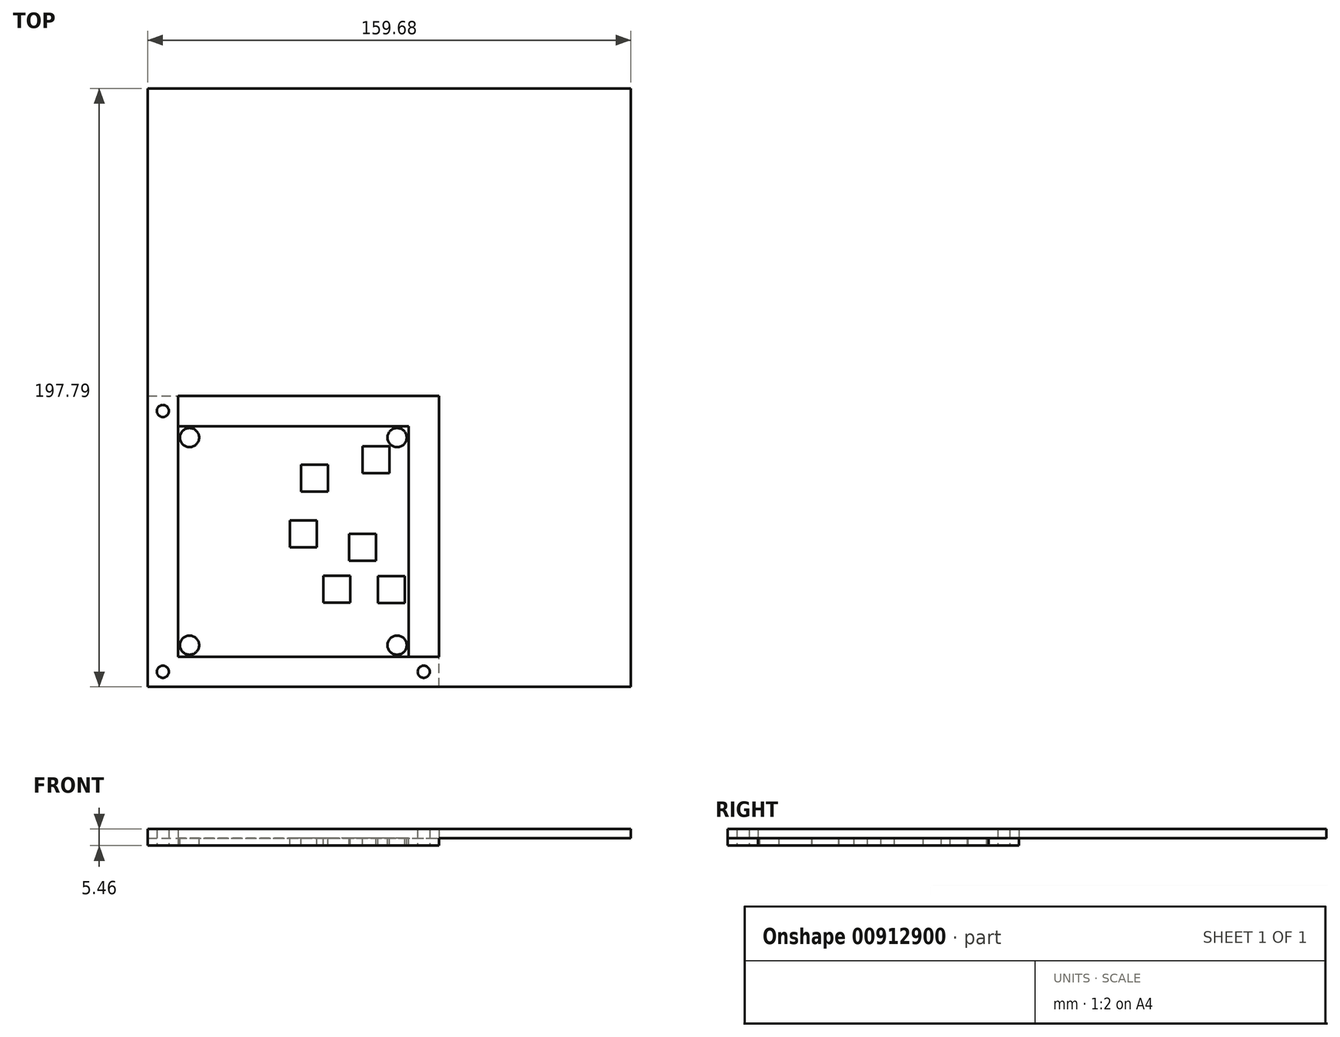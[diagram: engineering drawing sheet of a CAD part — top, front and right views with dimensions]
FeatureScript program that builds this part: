
annotation { "Feature Type Name" : "Feature", "Feature Type Description" : "" }
export const myFeature = defineFeature(function(context is Context, id is Id, definition is map)
    precondition{}
    {
        {
            var Q0;
            Q0=qCreatedBy(makeId("Top.planeOp"),FACE);
            var sketch = newSketch(context, id + "F0", { "sketchPlane" : qUnion([Q0])});
            skLineSegment(sketch, "E0.bottom", {"start": v(-59.12, -65.9) * mm, "end": v(37.08, -65.9) * mm});
            skLineSegment(sketch, "E0.top", {"start": v(-59.12, 30.3) * mm, "end": v(37.08, 30.3) * mm});
            skLineSegment(sketch, "E0.left", {"start": v(-59.12, -65.9) * mm, "end": v(-59.12, 30.3) * mm});
            skLineSegment(sketch, "E0.right", {"start": v(37.08, -65.9) * mm, "end": v(37.08, 30.3) * mm});
            skLineSegment(sketch, "E1.bottom", {"start": v(-59.12, -65.9) * mm, "end": v(-49.12, -65.9) * mm});
            skLineSegment(sketch, "E1.top", {"start": v(-59.12, -55.9) * mm, "end": v(-49.12, -55.9) * mm});
            skLineSegment(sketch, "E1.left", {"start": v(-59.12, -65.9) * mm, "end": v(-59.12, -55.9) * mm});
            skLineSegment(sketch, "E1.right", {"start": v(-49.12, -65.9) * mm, "end": v(-49.12, -55.9) * mm});
            skLineSegment(sketch, "E2.bottom", {"start": v(-49.12, -55.9) * mm, "end": v(27.08, -55.9) * mm});
            skLineSegment(sketch, "E2.top", {"start": v(-49.12, 20.3) * mm, "end": v(27.08, 20.3) * mm});
            skLineSegment(sketch, "E2.left", {"start": v(-49.12, -55.9) * mm, "end": v(-49.12, 20.3) * mm});
            skLineSegment(sketch, "E2.right", {"start": v(27.08, -55.9) * mm, "end": v(27.08, 20.3) * mm});
            skLineSegment(sketch, "E3.bottom", {"start": v(37.08, -65.9) * mm, "end": v(27.08, -65.9) * mm});
            skLineSegment(sketch, "E3.top", {"start": v(37.08, -55.9) * mm, "end": v(27.08, -55.9) * mm});
            skLineSegment(sketch, "E3.left", {"start": v(37.08, -65.9) * mm, "end": v(37.08, -55.9) * mm});
            skLineSegment(sketch, "E3.right", {"start": v(27.08, -65.9) * mm, "end": v(27.08, -55.9) * mm});
            skLineSegment(sketch, "E4.bottom", {"start": v(37.08, 30.3) * mm, "end": v(27.08, 30.3) * mm});
            skLineSegment(sketch, "E4.top", {"start": v(37.08, 20.3) * mm, "end": v(27.08, 20.3) * mm});
            skLineSegment(sketch, "E4.left", {"start": v(37.08, 30.3) * mm, "end": v(37.08, 20.3) * mm});
            skLineSegment(sketch, "E4.right", {"start": v(27.08, 30.3) * mm, "end": v(27.08, 20.3) * mm});
            skLineSegment(sketch, "E5.bottom", {"start": v(-59.12, 30.3) * mm, "end": v(-49.12, 30.3) * mm});
            skLineSegment(sketch, "E5.top", {"start": v(-59.12, 20.3) * mm, "end": v(-49.12, 20.3) * mm});
            skLineSegment(sketch, "E5.left", {"start": v(-59.12, 30.3) * mm, "end": v(-59.12, 20.3) * mm});
            skLineSegment(sketch, "E5.right", {"start": v(-49.12, 30.3) * mm, "end": v(-49.12, 20.3) * mm});
            skLineSegment(sketch, "E6.bottom", {"start": v(-59.12, 20.3) * mm, "end": v(-54.12, 20.3) * mm});
            skLineSegment(sketch, "E6.left", {"start": v(-59.12, 20.3) * mm, "end": v(-59.12, 25.3) * mm});
            skLineSegment(sketch, "E7.bottom", {"start": v(37.08, 20.3) * mm, "end": v(32.08, 20.3) * mm});
            skLineSegment(sketch, "E7.left", {"start": v(37.08, 20.3) * mm, "end": v(37.08, 25.3) * mm});
            skLineSegment(sketch, "E8.bottom", {"start": v(-59.12, -65.9) * mm, "end": v(-54.12, -65.9) * mm});
            skLineSegment(sketch, "E8.left", {"start": v(-59.12, -65.9) * mm, "end": v(-59.12, -60.9) * mm});
            skLineSegment(sketch, "E9.bottom", {"start": v(37.08, -65.9) * mm, "end": v(32.08, -65.9) * mm});
            skLineSegment(sketch, "E9.left", {"start": v(37.08, -65.9) * mm, "end": v(37.08, -60.9) * mm});
            skCircle(sketch, "E10", {"center": v(-54.12, 25.3) * mm, "radius": 2 * mm});
            skCircle(sketch, "E11", {"center": v(32.08, 25.3) * mm, "radius": 2 * mm});
            skCircle(sketch, "E12", {"center": v(-54.12, -60.9) * mm, "radius": 2 * mm});
            skCircle(sketch, "E13", {"center": v(32.08, -60.9) * mm, "radius": 2 * mm});
            skLineSegment(sketch, "E14.left", {"start": v(-49.12, -55.9) * mm, "end": v(-49.12, -55.65) * mm});
            skLineSegment(sketch, "E14.right", {"start": v(27.08, -55.9) * mm, "end": v(27.08, -55.65) * mm});
            skLineSegment(sketch, "E15.bottom", {"start": v(-49.12, 20.3) * mm, "end": v(-48.87, 20.3) * mm});
            skLineSegment(sketch, "E15.top", {"start": v(-49.12, -55.9) * mm, "end": v(-48.87, -55.9) * mm});
            skLineSegment(sketch, "E16.left", {"start": v(-49.12, 20.3) * mm, "end": v(-49.12, 20.05) * mm});
            skLineSegment(sketch, "E16.right", {"start": v(27.08, 20.3) * mm, "end": v(27.08, 20.05) * mm});
            skLineSegment(sketch, "E17.bottom", {"start": v(27.08, 20.3) * mm, "end": v(26.82, 20.3) * mm});
            skLineSegment(sketch, "E17.top", {"start": v(27.08, -55.9) * mm, "end": v(26.82, -55.9) * mm});
            skLineSegment(sketch, "E17.left", {"start": v(27.08, 20.3) * mm, "end": v(27.08, -55.9) * mm});
            skLineSegment(sketch, "E18.bottom", {"start": v(-49.12, -55.9) * mm, "end": v(-45.19, -55.9) * mm});
            skLineSegment(sketch, "E19.left", {"start": v(-49.12, -55.9) * mm, "end": v(-49.12, -54.15) * mm});
            skLineSegment(sketch, "E20.left", {"start": v(-49.12, -55.9) * mm, "end": v(-49.12, -51.96) * mm});
            skLineSegment(sketch, "E21.left", {"start": v(27.08, -55.9) * mm, "end": v(27.08, -51.96) * mm});
            skLineSegment(sketch, "E22.bottom", {"start": v(27.2, -55.9) * mm, "end": v(27.08, -55.9) * mm});
            skLineSegment(sketch, "E23.bottom", {"start": v(27.08, -55.9) * mm, "end": v(23.14, -55.9) * mm});
            skLineSegment(sketch, "E24.left", {"start": v(-49.12, 20.3) * mm, "end": v(-49.12, 16.36) * mm});
            skLineSegment(sketch, "E25.bottom", {"start": v(-49.12, 20.3) * mm, "end": v(-45.19, 20.3) * mm});
            skLineSegment(sketch, "E26.bottom", {"start": v(27.32, 20.3) * mm, "end": v(27.08, 20.3) * mm});
            skLineSegment(sketch, "E26.left", {"start": v(27.08, 20.43) * mm, "end": v(27.08, 20.3) * mm});
            skLineSegment(sketch, "E26.right", {"start": v(27.32, 20.43) * mm, "end": v(27.32, 20.3) * mm});
            skLineSegment(sketch, "E27.left", {"start": v(27.08, 20.3) * mm, "end": v(27.08, 16.36) * mm});
            skLineSegment(sketch, "E28.top", {"start": v(27.08, 20.3) * mm, "end": v(23.14, 20.3) * mm});
            skLineSegment(sketch, "E28.left", {"start": v(27.08, 20.05) * mm, "end": v(27.08, 20.3) * mm});
            skCircle(sketch, "E29", {"center": v(-45.32, 16.5) * mm, "radius": 3.18 * mm});
            skCircle(sketch, "E30", {"center": v(23.28, -52.1) * mm, "radius": 3.18 * mm});
            skCircle(sketch, "E31", {"center": v(23.28, 16.5) * mm, "radius": 3.18 * mm});
            skCircle(sketch, "E32", {"center": v(-45.32, -52.1) * mm, "radius": 3.17 * mm});
            skLineSegment(sketch, "E33.bottom", {"start": v(27.08, -55.9) * mm, "end": v(-0.86, -55.9) * mm});
            skLineSegment(sketch, "E33.left", {"start": v(27.08, -55.9) * mm, "end": v(27.08, -1.3) * mm});
            skLineSegment(sketch, "E34.bottom", {"start": v(0.4, -1.3) * mm, "end": v(-8.48, -1.3) * mm});
            skLineSegment(sketch, "E34.top", {"start": v(0.4, 7.6) * mm, "end": v(-8.48, 7.6) * mm});
            skLineSegment(sketch, "E34.left", {"start": v(0.4, -1.3) * mm, "end": v(0.4, 7.6) * mm});
            skLineSegment(sketch, "E34.right", {"start": v(-8.48, -1.3) * mm, "end": v(-8.48, 7.6) * mm});
            skLineSegment(sketch, "E35.bottom", {"start": v(27.08, -55.9) * mm, "end": v(-4.5, -55.9) * mm});
            skLineSegment(sketch, "E35.left", {"start": v(27.08, -55.9) * mm, "end": v(27.08, -19.7) * mm});
            skLineSegment(sketch, "E36.bottom", {"start": v(-3.23, -19.7) * mm, "end": v(-12.12, -19.7) * mm});
            skLineSegment(sketch, "E36.top", {"start": v(-3.23, -10.82) * mm, "end": v(-12.12, -10.82) * mm});
            skLineSegment(sketch, "E36.left", {"start": v(-3.23, -19.7) * mm, "end": v(-3.23, -10.82) * mm});
            skLineSegment(sketch, "E36.right", {"start": v(-12.12, -19.7) * mm, "end": v(-12.12, -10.82) * mm});
            skLineSegment(sketch, "E37.bottom", {"start": v(27.08, -55.9) * mm, "end": v(6.55, -55.9) * mm});
            skLineSegment(sketch, "E37.left", {"start": v(27.08, -55.9) * mm, "end": v(27.08, -38) * mm});
            skLineSegment(sketch, "E38.bottom", {"start": v(7.82, -38) * mm, "end": v(-1.07, -38) * mm});
            skLineSegment(sketch, "E38.top", {"start": v(7.82, -29.1) * mm, "end": v(-1.07, -29.1) * mm});
            skLineSegment(sketch, "E38.left", {"start": v(7.82, -38) * mm, "end": v(7.82, -29.1) * mm});
            skLineSegment(sketch, "E38.right", {"start": v(-1.07, -38) * mm, "end": v(-1.07, -29.1) * mm});
            skLineSegment(sketch, "E39.bottom", {"start": v(27.08, -55.9) * mm, "end": v(23.52, -55.9) * mm});
            skLineSegment(sketch, "E39.left", {"start": v(27.08, -55.9) * mm, "end": v(27.08, 4.7) * mm});
            skLineSegment(sketch, "E40.bottom", {"start": v(20.73, 4.7) * mm, "end": v(11.84, 4.7) * mm});
            skLineSegment(sketch, "E40.top", {"start": v(20.73, 13.6) * mm, "end": v(11.84, 13.6) * mm});
            skLineSegment(sketch, "E40.left", {"start": v(11.84, 4.7) * mm, "end": v(11.84, 13.6) * mm});
            skLineSegment(sketch, "E40.right", {"start": v(20.73, 4.7) * mm, "end": v(20.73, 13.6) * mm});
            skPoint(sketch, "E41.oppositeSnap0", {"position": v(16.28, 13.6) * mm});
            skLineSegment(sketch, "E41.bottom", {"start": v(27.08, -55.9) * mm, "end": v(24.54, -55.9) * mm});
            skLineSegment(sketch, "E41.left", {"start": v(27.08, -55.9) * mm, "end": v(27.08, -24.15) * mm});
            skLineSegment(sketch, "E42.bottom", {"start": v(16.28, -24.15) * mm, "end": v(7.4, -24.15) * mm});
            skLineSegment(sketch, "E42.top", {"start": v(16.28, -15.26) * mm, "end": v(7.4, -15.26) * mm});
            skLineSegment(sketch, "E42.left", {"start": v(16.28, -24.15) * mm, "end": v(16.28, -15.26) * mm});
            skLineSegment(sketch, "E42.right", {"start": v(7.4, -24.15) * mm, "end": v(7.4, -15.26) * mm});
            skLineSegment(sketch, "E43.bottom", {"start": v(27.08, -55.9) * mm, "end": v(26.57, -55.9) * mm});
            skLineSegment(sketch, "E43.left", {"start": v(27.08, -55.9) * mm, "end": v(27.08, -38.12) * mm});
            skLineSegment(sketch, "E44.bottom", {"start": v(25.8, -38.12) * mm, "end": v(16.92, -38.12) * mm});
            skLineSegment(sketch, "E44.top", {"start": v(25.8, -29.23) * mm, "end": v(16.92, -29.23) * mm});
            skLineSegment(sketch, "E44.left", {"start": v(25.8, -38.12) * mm, "end": v(25.8, -29.23) * mm});
            skLineSegment(sketch, "E44.right", {"start": v(16.92, -38.12) * mm, "end": v(16.92, -29.23) * mm});
            skLineSegment(sketch, "E45.top", {"start": v(-59.12, -30.5) * mm, "end": v(-49.12, -30.5) * mm});
            skLineSegment(sketch, "E45.left", {"start": v(-59.12, 20.3) * mm, "end": v(-59.12, -30.5) * mm});
            skLineSegment(sketch, "E45.right", {"start": v(-49.12, 20.3) * mm, "end": v(-49.12, -30.5) * mm});
            skLineSegment(sketch, "E46", {"start": v(27.08, -38.12) * mm, "end": v(25.8, -38.12) * mm});
            skLineSegment(sketch, "E47.bottom", {"start": v(-59.12, -65.9) * mm, "end": v(100.56, -65.9) * mm});
            skLineSegment(sketch, "E47.top", {"start": v(-59.12, 131.89) * mm, "end": v(100.56, 131.89) * mm});
            skLineSegment(sketch, "E47.left", {"start": v(-59.12, -65.9) * mm, "end": v(-59.12, 131.89) * mm});
            skLineSegment(sketch, "E47.right", {"start": v(100.56, -65.9) * mm, "end": v(100.56, 131.89) * mm});
            skSolve(sketch);
        }
        {
            var Q0;
            Q0=makeQuery(id+"F0.imprint","IMPRINT",FACE,{"disambiguationData":[TD([[makeQuery(id+"F0.imprint","IMPRINT",EDGE,{"derivedFrom":sQuery(id+"F0.wireOp",EDGE,"E0.top")}),-1.0]])]});
            var Q1;
            Q1=makeQuery(id+"F0.imprint","IMPRINT",FACE,{"disambiguationData":[TD([[makeQuery(id+"F0.imprint","IMPRINT",EDGE,{"derivedFrom":sQuery(id+"F0.wireOp",EDGE,"E5.bottom")}),-1.0]])]});
            var Q2;
            Q2=makeQuery(id+"F0.imprint","IMPRINT",FACE,{"disambiguationData":[TD([[makeQuery(id+"F0.imprint","IMPRINT",EDGE,{"derivedFrom":sQuery(id+"F0.wireOp",EDGE,"E0.left")}),-1.0]])]});
            var Q3;
            Q3=makeQuery(id+"F0.imprint","IMPRINT",FACE,{"disambiguationData":[TD([[makeQuery(id+"F0.imprint","IMPRINT",EDGE,{"derivedFrom":sQuery(id+"F0.wireOp",EDGE,"E0.right")}),1.0]])]});
            var Q4;
            Q4=makeQuery(id+"F0.imprint","IMPRINT",FACE,{"disambiguationData":[TD([[makeQuery(id+"F0.imprint","IMPRINT",EDGE,{"derivedFrom":sQuery(id+"F0.wireOp",EDGE,"E4.bottom")}),1.0]])]});
            var Q5;
            Q5=makeQuery(id+"F0.imprint","IMPRINT",FACE,{"disambiguationData":[TD([[makeQuery(id+"F0.imprint","IMPRINT",EDGE,{"derivedFrom":sQuery(id+"F0.wireOp",EDGE,"E3.bottom")}),-1.0]])]});
            var Q6;
            Q6=makeQuery(id+"F0.imprint","IMPRINT",FACE,{"disambiguationData":[TD([[makeQuery(id+"F0.imprint","IMPRINT",EDGE,{"derivedFrom":sQuery(id+"F0.wireOp",EDGE,"E0.bottom")}),1.0]])]});
            var Q7;
            Q7=makeQuery(id+"F0.imprint","IMPRINT",FACE,{"disambiguationData":[TD([[makeQuery(id+"F0.imprint","IMPRINT",EDGE,{"derivedFrom":sQuery(id+"F0.wireOp",EDGE,"E1.bottom")}),1.0]])]});
            var Q8;
            {var subQ4=sQuery(id+"F0.wireOp",EDGE,"E1.top");Q8=makeQuery(id+"F0.imprint","IMPRINT",FACE,{"disambiguationData":[TD([[makeQuery(id+"F0.imprint","IMPRINT",EDGE,{"derivedFrom":subQ4}),1.0]])]});}
            var Q9;
            {var subQ4=sQuery(id+"F0.wireOp",EDGE,"E1.top");Q9=makeQuery(id+"F0.imprint","IMPRINT",FACE,{"disambiguationData":[TD([[makeQuery(id+"F0.imprint","IMPRINT",EDGE,{"derivedFrom":subQ4}),-1.0]])]});}
            var Q10;
            {var subQ11=sQuery(id+"F0.wireOp",EDGE,"E1.right");Q10=makeQuery(id+"F0.imprint","IMPRINT",FACE,{"disambiguationData":[TD([[makeQuery(id+"F0.imprint","IMPRINT",EDGE,{"derivedFrom":subQ11}),-1.0]])]});}
            var Q11;
            Q11=makeQuery(id+"F0.imprint","IMPRINT",FACE,{"disambiguationData":[TD([[makeQuery(id+"F0.imprint","IMPRINT",EDGE,{"derivedFrom":sQuery(id+"F0.wireOp",EDGE,"E3.top")}),1.0]])]});
            extrude(context, id + "F1", {"entities" : qUnion([Q0, Q1, Q2, Q3, Q4, Q5, Q6, Q7, Q8, Q9, Q10, Q11]), "depth" : 3 * mm, "offsetDistance" : 25.4 * mm});
        }
        {
            var Q0;
            Q0=makeQuery(id+"F0.imprint","IMPRINT",FACE,{"disambiguationData":[TD([[makeQuery(id+"F0.imprint","IMPRINT",EDGE,{"derivedFrom":sQuery(id+"F0.wireOp",EDGE,"E4.bottom")}),1.0]])]});
            var Q1;
            Q1=makeQuery(id+"F0.imprint","IMPRINT",FACE,{"disambiguationData":[TD([[makeQuery(id+"F0.imprint","IMPRINT",EDGE,{"derivedFrom":sQuery(id+"F0.wireOp",EDGE,"E0.right")}),1.0]])]});
            var Q2;
            Q2=makeQuery(id+"F0.imprint","IMPRINT",FACE,{"disambiguationData":[TD([[makeQuery(id+"F0.imprint","IMPRINT",EDGE,{"derivedFrom":sQuery(id+"F0.wireOp",EDGE,"E0.top")}),-1.0]])]});
            var Q3;
            Q3=makeQuery(id+"F0.imprint","IMPRINT",FACE,{"disambiguationData":[TD([[makeQuery(id+"F0.imprint","IMPRINT",EDGE,{"derivedFrom":sQuery(id+"F0.wireOp",EDGE,"E5.bottom")}),-1.0]])]});
            var Q4;
            {var subQ1=sQuery(id+"F0.wireOp",EDGE,"E45.top");Q4=makeQuery(id+"F0.imprint","IMPRINT",FACE,{"disambiguationData":[TD([[makeQuery(id+"F0.imprint","IMPRINT",EDGE,{"derivedFrom":subQ1}),1.0]])]});}
            var Q5;
            Q5=makeQuery(id+"F0.imprint","IMPRINT",FACE,{"disambiguationData":[TD([[makeQuery(id+"F0.imprint","IMPRINT",EDGE,{"derivedFrom":sQuery(id+"F0.wireOp",EDGE,"E0.left")}),-1.0]])]});
            var Q6;
            Q6=makeQuery(id+"F0.imprint","IMPRINT",FACE,{"disambiguationData":[TD([[makeQuery(id+"F0.imprint","IMPRINT",EDGE,{"derivedFrom":sQuery(id+"F0.wireOp",EDGE,"E1.bottom")}),1.0]])]});
            var Q7;
            Q7=makeQuery(id+"F0.imprint","IMPRINT",FACE,{"disambiguationData":[TD([[makeQuery(id+"F0.imprint","IMPRINT",EDGE,{"derivedFrom":sQuery(id+"F0.wireOp",EDGE,"E0.bottom")}),1.0]])]});
            var Q8;
            Q8=makeQuery(id+"F0.imprint","IMPRINT",FACE,{"disambiguationData":[TD([[makeQuery(id+"F0.imprint","IMPRINT",EDGE,{"derivedFrom":sQuery(id+"F0.wireOp",EDGE,"E3.bottom")}),-1.0]])]});
            var Q9;
            {var subQ24=sQuery(id+"F0.wireOp",EDGE,"E2.left");Q9=makeQuery(id+"F0.imprint","IMPRINT",FACE,{"disambiguationData":[TD([[makeQuery(id+"F0.imprint","IMPRINT",EDGE,{"derivedFrom":subQ24}),-1.0]])]});}
            var Q10;
            {var subQ4=sQuery(id+"F0.wireOp",EDGE,"E1.top");Q10=makeQuery(id+"F0.imprint","IMPRINT",FACE,{"disambiguationData":[TD([[makeQuery(id+"F0.imprint","IMPRINT",EDGE,{"derivedFrom":subQ4}),1.0]])]});}
            var Q11;
            {var subQ4=sQuery(id+"F0.wireOp",EDGE,"E1.top");Q11=makeQuery(id+"F0.imprint","IMPRINT",FACE,{"disambiguationData":[TD([[makeQuery(id+"F0.imprint","IMPRINT",EDGE,{"derivedFrom":subQ4}),-1.0]])]});}
            var Q12;
            {var subQ11=sQuery(id+"F0.wireOp",EDGE,"E1.right");Q12=makeQuery(id+"F0.imprint","IMPRINT",FACE,{"disambiguationData":[TD([[makeQuery(id+"F0.imprint","IMPRINT",EDGE,{"derivedFrom":subQ11}),-1.0]])]});}
            var Q13;
            Q13=makeQuery(id+"F0.imprint","IMPRINT",FACE,{"disambiguationData":[TD([[makeQuery(id+"F0.imprint","IMPRINT",EDGE,{"derivedFrom":sQuery(id+"F0.wireOp",EDGE,"E3.top")}),1.0]])]});
            extrude(context, id + "F2", {"entities" : qUnion([Q0, Q1, Q2, Q3, Q4, Q5, Q6, Q7, Q8, Q9, Q10, Q11, Q12, Q13]), "operationType" : NewBodyOperationType.ADD, "oppositeDirection" : true, "depth" : 2.46 * mm, "offsetDistance" : 25.4 * mm});
        }
        {
            var Q0;
            Q0 = qSketchRegion(id + "F0", true);
            extrude(context, id + "F3", {"entities" : qUnion([Q0]), "operationType" : NewBodyOperationType.ADD, "depth" : 3 * mm, "offsetDistance" : 25 * mm});
        }
    });
